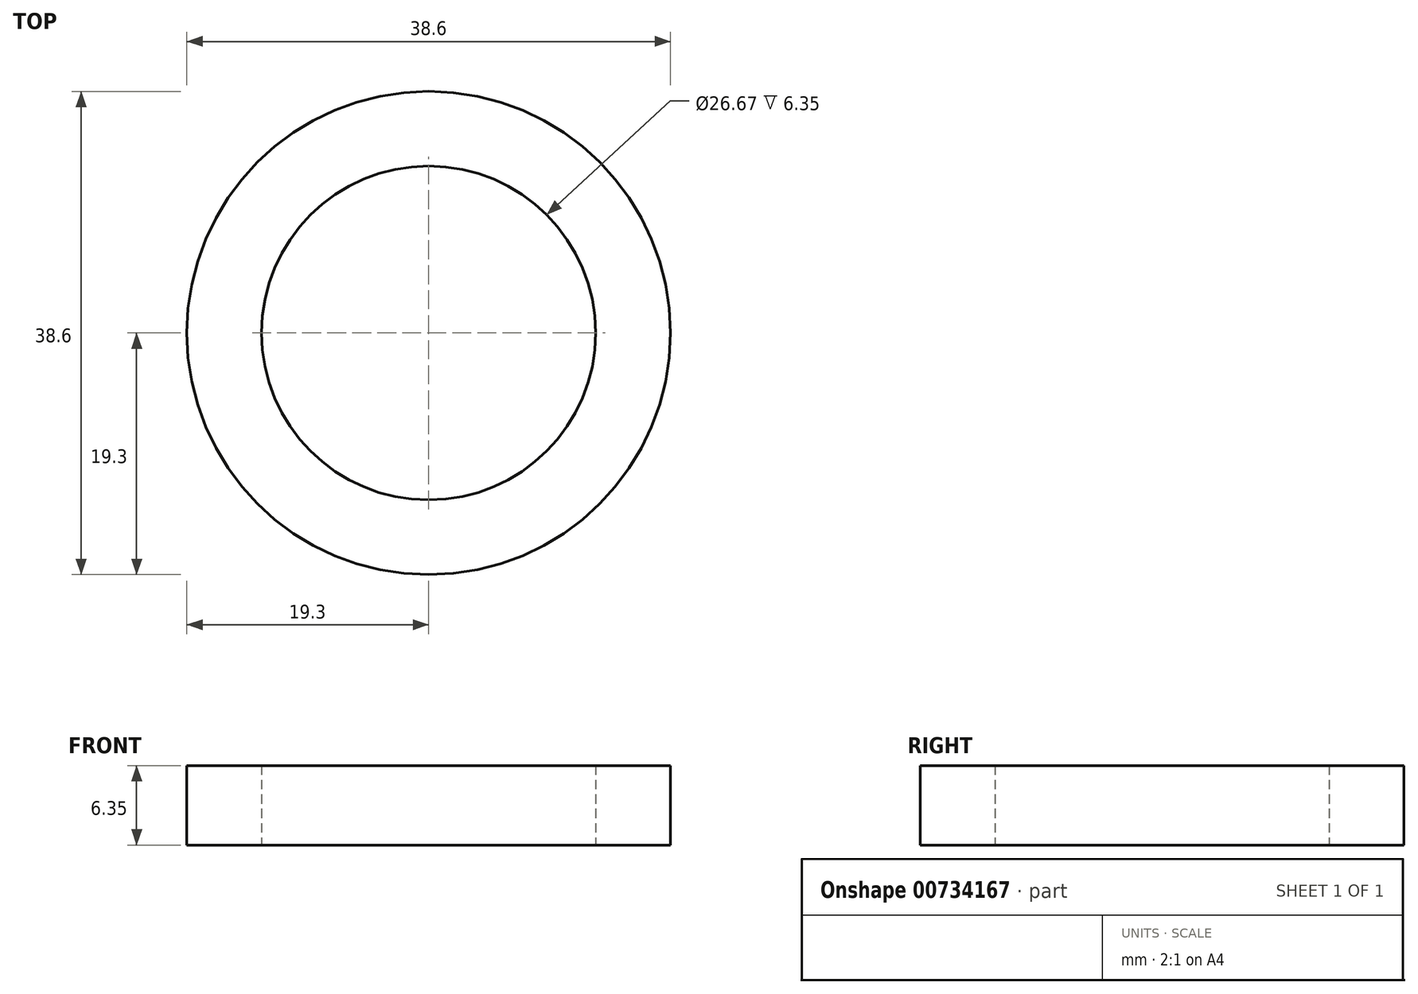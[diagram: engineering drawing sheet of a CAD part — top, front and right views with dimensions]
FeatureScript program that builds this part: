
annotation { "Feature Type Name" : "Feature", "Feature Type Description" : "" }
export const myFeature = defineFeature(function(context is Context, id is Id, definition is map)
    precondition{}
    {
        {
            var Q0;
            Q0=qCreatedBy(makeId("Top.planeOp"),FACE);
            var sketch = newSketch(context, id + "F0", { "sketchPlane" : qUnion([Q0])});
            skCircle(sketch, "E0", {"center": v(0, 0) * mm, "radius": 13.34 * mm});
            skCircle(sketch, "E1", {"center": v(0, 0) * mm, "radius": 19.3 * mm});
            skSolve(sketch);
        }
        {
            var Q0;
            Q0=makeQuery(id+"F0.imprint","IMPRINT",FACE,{"disambiguationData":[TD([[makeQuery(id+"F0.imprint","IMPRINT",EDGE,{"derivedFrom":sQuery(id+"F0.wireOp",EDGE,"E0")}),-1.0]])]});
            extrude(context, id + "F1", {"entities" : qUnion([Q0]), "depth" : 6.35 * mm, "offsetDistance" : 25.4 * mm});
        }
    });
